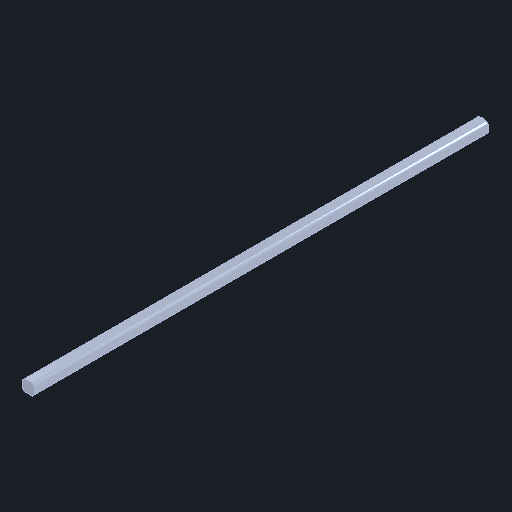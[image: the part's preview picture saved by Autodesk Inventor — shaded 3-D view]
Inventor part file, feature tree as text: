
AUTODESK INVENTOR PART (.ipt)
format: ipt  version: 2025 (Build 290162000, 162)  size: 174,592 bytes
history: native  units: in
note: dims shown in document units (in); Inventor stores cm internally (conversion verified against a paired STEP export)
features: other x50, extrude x2, sketch x2, thicken_offset x1
ambient origin geometry x8: Origin, YZ Plane, XZ Plane, XY Plane, X Axis, Y Axis, Z Axis, Center Point
bodies: Solid1 (feature_tree)
feature tree (55):
  other  "Table"
  other  "Shaft HS 0.5 in"
  other  "Shaft HS 1.0 in"
  other  "Shaft HS 1.5 in"
  other  "Shaft HS 2.0 in"
  other  "Shaft HS 2.5 in"
  other  "Shaft HS 3.0 in"
  other  "Shaft HS 3.5 in"
  other  "Shaft HS 4.0 in"
  other  "Shaft HS 4.5 in"
  other  "Shaft HS 5.0 in"
  other  "Shaft HS 5.5 in"
  other  "Shaft HS 6.0 in"
  other  "Shaft HS 6.5 in"
  other  "Shaft HS 7.0 in"
  other  "Shaft HS 7.5 in"
  other  "Shaft HS 8.0 in"
  other  "Shaft HS 8.5 in"
  other  "Shaft HS 9.0 in"
  other  "Shaft HS 9.5 in"
  other  "Shaft HS 10.0 in"
  other  "Shaft HS 10.5 in"
  other  "Shaft HS 11.0 in"
  other  "Shaft HS 11.5 in"
  other  "Shaft HS 12.0 in"
  other  "Shaft HS 12.5 in"
  other  "Shaft HS 13.0 in"
  other  "Shaft HS 13.5 in"
  other  "Shaft HS 14.0 in"
  other  "Shaft HS 14.5 in"
  other  "Shaft HS 15.0 in"
  other  "Shaft HS 15.5 in"
  other  "Shaft HS 16.0 in"
  other  "Shaft HS 16.5 in"
  other  "Shaft HS 17.0 in"
  other  "Shaft HS 17.5 in"
  other  "Shaft HS 18.0 in"
  other  "Shaft HS 18.5 in"
  other  "Shaft HS 19.0 in"
  other  "Shaft HS 19.5 in"
  other  "Shaft HS 20.0 in"
  other  "Shaft HS 20.5 in"
  other  "Shaft HS 21.0 in"
  other  "Shaft HS 21.5 in"
  other  "Shaft HS 22.0 in"
  other  "Shaft HS 22.5 in"
  other  "Shaft HS 23.0 in"
  other  "Shaft HS 23.5 in"
  other  "Shaft HS 24.0 in"
  extrude  "Extrusion1"  Depth=12.1875in
  thicken_offset  "Thicken1"
  extrude  "Extrusion2"  Depth=14.125in
  sketch  "Sketch2"  dims[d0=0.0625in d1=0.0in d2=12.1875in]
  sketch  "Sketch3"  dims[d3=12.125in d4=14.125in d5=0.0in]
  other  "Cut-Revolve3"
